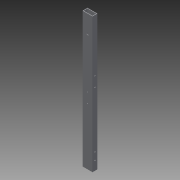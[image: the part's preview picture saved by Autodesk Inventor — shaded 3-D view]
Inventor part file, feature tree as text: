
AUTODESK INVENTOR PART (.ipt)
format: ipt  version: 2013 (Build 170138000, 138)  size: 150,528 bytes
history: native  units: in
note: dims shown in document units (in); Inventor stores cm internally (conversion verified against a paired STEP export)
features: sketch x7, extrude x6, hole x1
ambient origin geometry x8: Origin, YZ Plane, XZ Plane, XY Plane, X Axis, Y Axis, Z Axis, Center Point
bodies: Solid1 (feature_tree)
feature tree (14):
  extrude  "Extrusion1"  Depth=1.0in
  extrude  "Extrusion2"  Depth=0.75in
  extrude  "Extrusion4"  Depth=1.0in
  extrude  "Extrusion6"  Depth=0.5in
  extrude  "Extrusion8"  Depth=0.5in TaperAngle=0.0deg
  extrude  "Extrusion9"  Depth=10.5in
  hole  "Hole1"  [1 undecoded]
  sketch  "Sketch1"  dims[d0=2.0in d1=1.0in]
  sketch  "Sketch2"  dims[d2=1.75in d3=0.75in]
  sketch  "Sketch4"  dims[d4=24.0in d5=0.0in d6=1.0in]
  sketch  "Sketch6"  dims[d7=1.0in d8=0.5in]
  sketch  "Sketch7"  dims[d9=24.0in d10=0.0in d25=0.5in d26=0.0in]
  sketch  "Sketch8"  dims[d35=2.5in d36=0.0in d37=10.5in]
  sketch  "Sketch9"  dims[d38=90.0deg d39=0.25in d40=2.0in d41=2.0in d42=90.0deg d43=0.25in d44=0.25in d47=2.0in d48=0.0in d49=13.543in d50=90.0deg d51=2.0in d52=180.0deg d53=0.25in d54=0.25in d55=2.0in d56=0.0in d57=3.313in d58=1.5in d59=90.0deg d60=0.25in d61=0.75in d62=0.375in d63=0.25in d64=0.5635in d65=1.0in d66=0.8108in]
note: 1 required parameter value undecoded (feature->parameter linkage not recoverable at this tier; creation-order binding heuristic only, values carry confidence <= 0.55)
